# Revit family: LK4408BFTER
name_source: partatom
category: Plumbing Fixtures
units: mm (PartAtom-declared; Revit-internal decimal feet)

## family parameters
Always vertical = Yes
Cut with Voids When Loaded = No
OmniClass Number = 23.45.00.00
OmniClass Title = Sanitary, Laundry, and Cleaning Equipment
Part Type = Normal
Room Calculation Point = No
Round Connector Dimension = Use Diameter
Shared = No
Work Plane-Based = No

## types (12) — shared parameters
Activation by = Mechanical Bottle Filler Button With Mechanical Front Bubbler Button
Approx. Shipping Weight = 176 lbs.
BASIN_MATERIAL = Metal - Steel - Stainless - Chrome
BOTTLE_SHAPE MATERIAL = Metal - Steel - Stainless - Chrome
Bubbler Style = Vandal Resistant
CW Connection = Yes
Chilling Option = Non-refrigerated
DRAIN_MATERIAL = Metal - Steel - Stainless - Chrome
Description = Elkay Outdoor EZH2O Bottle Filling Station Wall Mount Non-Filtered Non-Refrigerated
Dimensions (L x W x H) = 21-1/4inch x 21-7/16inch x 33-1/2inch
Drain_Pipe 1 1/2" = 38 mm
HW Connection = No
Inlet_Pipe = 10 mm  [stored 0.0328084 ft]
Installation Location = Outdoor
Manufacturer = Elkay
Model = LK4408BF
Mounting Type = Wall Mount (On Wall)
No. of Stations Served = 2
PUSH_BUTTON_MATERIAL = Metal - Steel - Stainless - Chrome
Power = No Electrical Required
SINK_MATERIAL = Metal - Steel - Stainless - Chrome
Special Features = 316 Stainless, Heavy Duty Vandal Resistant
Vent Connection = No
Version = 1.0.0.0
Waste Connection = Yes

## per-type parameters (varying)
| type | Assembly Code | FOUNDATION_BODY_MATERIAL | Finish | URL |
| Evergreen(EVG) |  | Evergreen (EVG) | Evergreen |  |
| Blue(BLU) |  | Blue (BLU) | Blue |  |
| Purple(PUR) |  | Purple (PUR) | Purple |  |
| Red(RED) |  | Red(RED) | Red |  |
| Terracotta(TER) |  | Terracotta(TER) | Terracotta |  |
| Orange(ORN) |  | Orange(ORN) | Orange |  |
| Yellow(YLW) |  | Yellow(YLW) | Yellow(YLW) |  |
| Black(BLK) | D2010800 | Black(BLK) | Black | http://www.elkay.com |
| Brown(BRN) |  | Brown(BRN) | Brown |  |
| Gray(GRY) |  | Grey(GRY) | Gray |  |
| Beige(BGE) |  | Beige(BGE) | Beige |  |
| White(WHT) |  | White(WHT) | White |  |

note: [stored X ft] marks values corroborated as IEEE doubles in the binary element streams (Revit-internal decimal feet)

## geometry (parser evidence)
native form markers: Blend x2, Sweep x28
no freeform markers — native parametric forms only
